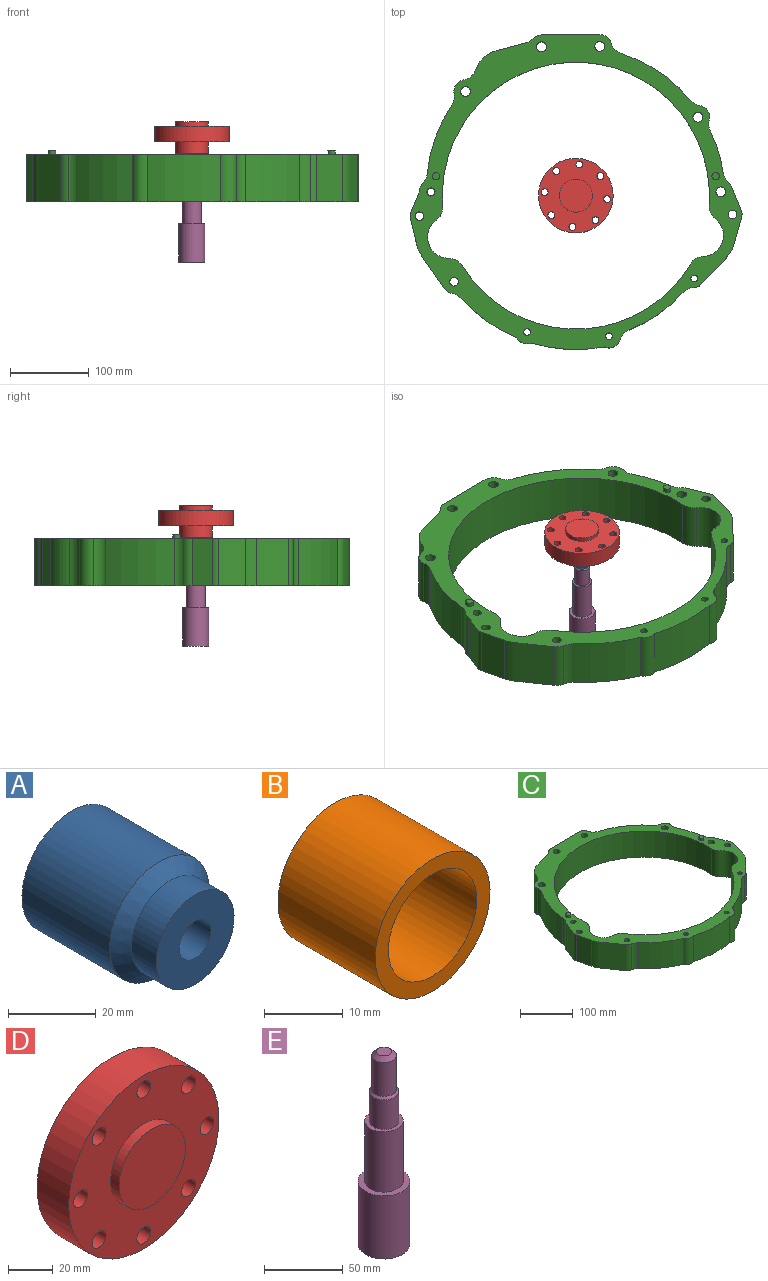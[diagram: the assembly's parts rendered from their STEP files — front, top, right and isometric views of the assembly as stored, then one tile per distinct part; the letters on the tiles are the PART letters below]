
ASSEMBLY  parts=5 mates=4
PART A: 10 faces, bbox 32x39.7x32 mm
  f0: plane 25x25mm, normal (0,-1,0), area 409.2mm2, adj f1,f9
  f1: cylinder r=5.1mm len=12.2mm, axis (0,-1,0), area 390.9mm2, adj f0,f2
  f2: plane 16.5x16.5mm, normal (0,1,0), area 132.1mm2, adj f1,f3
  f3: cylinder r=8.25mm len=16.5mm, axis (0,-1,0), area 518.4mm2, adj f2,f4
  f4: plane 20.65x20.65mm, normal (0,1,0), area 121.1mm2, adj f3,f5
  f5: cylinder r=10.33mm len=20.65mm, axis (0,-1,0), area 1135.3mm2, adj f4,f6
  f6: plane 32x32mm, normal (0,1,0), area 469.3mm2, adj f5,f7
  f7: cylinder r=16mm len=32mm, axis (0,-1,0), area 2835mm2, adj f6,f8
  f8: cone r=12.5mm half-angle=45deg, axis (0,1,0), area 443.2mm2, adj f7,f9
  f9: cylinder r=12.5mm len=25mm, axis (0,-1,0), area 628.3mm2, adj f0,f8
PART B: 4 faces, bbox 20.7x17.5x20.7 mm
  f0: cylinder r=10.33mm len=20.65mm, axis (0,-1,0), area 1135.3mm2, adj f1,f3
  f1: plane 20.65x20.65mm, normal (0,-1,0), area 136.4mm2, adj f0,f2
  f2: cylinder r=7.95mm len=17.5mm, axis (0,-1,0), area 874.1mm2, adj f1,f3
  f3: plane 20.65x20.65mm, normal (0,1,0), area 136.4mm2, adj f0,f2
PART C: 70 faces, bbox 422.8x401.2x65 mm
  f0: cylinder r=4.75mm len=55mm, axis (0,0,1), area 1641.5mm2, adj f62,f69
  f1: cylinder r=4.75mm len=55mm, axis (0,0,1), area 1641.5mm2, adj f62,f66
  f2: cylinder r=15mm len=60mm, axis (0,0,1), area 1165.5mm2, adj f3,f60,f62,f63
  f3: cylinder r=20mm len=60mm, axis (0,0,1), area 1172.4mm2, adj f2,f4,f62,f63
  f4: cylinder r=190mm len=88.05mm, axis (0,0,1), area 6458.4mm2, adj f3,f5,f62,f63
  f5: cylinder r=20mm len=60mm, axis (0,0,1), area 844.1mm2, adj f4,f6,f62,f63
  f6: cylinder r=15mm len=60mm, axis (0,0,1), area 1487.3mm2, adj f5,f7,f62,f63
  f7: cylinder r=20mm len=60mm, axis (0,0,1), area 844.1mm2, adj f6,f8,f62,f63
  f8: cylinder r=190mm len=60mm, axis (0,0,1), area 3403.2mm2, adj f7,f9,f62,f63
  f9: cylinder r=20mm len=60mm, axis (0,0,1), area 844.1mm2, adj f8,f10,f62,f63
  f10: cylinder r=15mm len=60mm, axis (0,0,1), area 421.9mm2, adj f9,f11,f62,f63
  f11: plane 60x30.04mm, normal (0.93,0.38,0), area 1944.6mm2, adj f10,f12,f62,f63
  f12: cylinder r=12mm len=60mm, axis (0,0,1), area 475.6mm2, adj f11,f13,f62,f63
  f13: plane 60x34.57mm, normal (0.96,-0.27,0), area 2155.9mm2, adj f12,f14,f62,f63
  f14: cylinder r=42mm len=60mm, axis (0,0,1), area 1222.6mm2, adj f13,f15,f62,f63
  f15: plane 60x34mm, normal (0.72,-0.69,0), area 2817.4mm2, adj f14,f16,f62,f63
  f16: cylinder r=11.25mm len=60mm, axis (0,0,1), area 534.3mm2, adj f15,f17,f62,f63
  f17: cylinder r=20mm len=60mm, axis (0,0,1), area 981.4mm2, adj f16,f18,f62,f63
  f18: cylinder r=184mm len=68.46mm, axis (0,0,1), area 5045.7mm2, adj f17,f19,f62,f63
  f19: cylinder r=20mm len=60mm, axis (0,0,1), area 1062.5mm2, adj f18,f20,f62,f63
  f20: cylinder r=15mm len=60mm, axis (0,0,1), area 1515.6mm2, adj f19,f21,f62,f63
  f21: cylinder r=196mm len=92.59mm, axis (0,0,1), area 5616.6mm2, adj f20,f22,f62,f63
  f22: cylinder r=15mm len=60mm, axis (0,0,1), area 1293.7mm2, adj f21,f23,f62,f63
  f23: cylinder r=196mm len=70.76mm, axis (0,0,1), area 5248.8mm2, adj f22,f24,f62,f63
  f24: cylinder r=20mm len=60mm, axis (0,0,1), area 810.5mm2, adj f23,f25,f62,f63
  f25: cylinder r=15mm len=60mm, axis (0,0,1), area 718.6mm2, adj f24,f26,f62,f63
  f26: plane 60x41.39mm, normal (-0.82,-0.57,0), area 3024.7mm2, adj f25,f27,f62,f63
  f27: cylinder r=42mm len=60mm, axis (0,0,1), area 924mm2, adj f26,f28,f62,f63
  f28: plane 60x33.81mm, normal (-0.97,-0.24,0), area 2088.9mm2, adj f27,f29,f62,f63
  f29: cylinder r=12mm len=60mm, axis (0,0,1), area 455.1mm2, adj f28,f30,f62,f63
  f30: plane 60x26.3mm, normal (-0.92,0.38,0), area 1707mm2, adj f29,f31,f62,f63
  f31: cylinder r=15mm len=60mm, axis (0,0,1), area 703.8mm2, adj f30,f32,f62,f63
  f32: cylinder r=20mm len=60mm, axis (0,0,1), area 824.6mm2, adj f31,f33,f62,f63
  f33: cylinder r=190mm len=87.63mm, axis (0,0,1), area 5639mm2, adj f32,f34,f62,f63
  f34: cylinder r=20mm len=60mm, axis (0,0,1), area 927.7mm2, adj f33,f35,f62,f63
  f35: cylinder r=15mm len=60mm, axis (0,0,1), area 1422.1mm2, adj f34,f36,f62,f63
  f36: cylinder r=20mm len=60mm, axis (0,0,1), area 1270.7mm2, adj f35,f37,f62,f63
  f37: cylinder r=38mm len=60mm, axis (0,0,1), area 2206.5mm2, adj f36,f38,f62,f63
  f38: plane 60x38.22mm, normal (-0.26,0.96,0), area 2376.4mm2, adj f37,f39,f62,f63
  f39: cylinder r=20mm len=60mm, axis (0,0,1), area 629.5mm2, adj f38,f40,f62,f63
  f40: cylinder r=15mm len=60mm, axis (0,0,1), area 703.9mm2, adj f39,f60,f62,f63
  f41: cylinder r=170mm len=340mm, axis (0,0,1), area 33542.8mm2, adj f42,f61,f62,f63
  f42: cylinder r=20mm len=60mm, axis (0,0,1), area 1223.2mm2, adj f41,f43,f62,f63
  f43: cylinder r=27mm len=60mm, axis (0,0,1), area 4072mm2, adj f42,f44,f62,f63
  f44: cylinder r=20mm len=60mm, axis (0,0,1), area 1223.2mm2, adj f43,f45,f62,f63
  f45: cylinder r=170mm len=290.68mm, axis (0,0,1), area 20920.2mm2, adj f44,f46,f62,f63
  f46: cylinder r=20mm len=60mm, axis (0,0,1), area 1181.3mm2, adj f45,f47,f62,f63
  f47: cylinder r=27mm len=60mm, axis (0,0,1), area 3948.7mm2, adj f46,f61,f62,f63
  f48: cylinder r=6.25mm len=60mm, axis (0,0,1), area 2356.2mm2, adj f62,f63
  f49: cylinder r=6.25mm len=60mm, axis (0,0,1), area 2356.2mm2, adj f62,f63
  f50: cylinder r=6.25mm len=60mm, axis (0,0,1), area 2356.2mm2, adj f62,f63
  f51: cylinder r=5.5mm len=60mm, axis (0,0,1), area 2073.5mm2, adj f62,f63
  f52: cylinder r=4.25mm len=60mm, axis (0,0,1), area 1602.2mm2, adj f62,f63
  f53: cylinder r=4.25mm len=60mm, axis (0,0,1), area 1602.2mm2, adj f62,f63
  f54: cylinder r=5.12mm len=60mm, axis (0,0,1), area 1932.1mm2, adj f62,f63
  f55: cylinder r=5.5mm len=60mm, axis (0,0,1), area 2073.5mm2, adj f62,f63
  f56: cylinder r=5.5mm len=60mm, axis (0,0,1), area 2073.5mm2, adj f62,f63
  f57: cylinder r=4.25mm len=60mm, axis (0,0,1), area 1602.2mm2, adj f62,f63
  f58: cylinder r=6.25mm len=60mm, axis (0,0,1), area 2356.2mm2, adj f62,f63
  f59: cylinder r=6.25mm len=60mm, axis (0,0,1), area 2356.2mm2, adj f62,f63
  f60: plane 74.32x60mm, normal (-0.01,1,0), area 4459.1mm2, adj f2,f40,f62,f63
  f61: cylinder r=20mm len=60mm, axis (0,0,1), area 1181.3mm2, adj f41,f47,f62,f63
  f62: plane 422.76x401.19mm, normal (0,0,-1), area 29010.6mm2, adj f0,f1,f2,f3,f4,f5,f6,f7
  f63: plane 422.76x401.19mm, normal (0,0,1), area 29010.6mm2, adj f2,f3,f4,f5,f6,f7,f8,f9
  f64: plane 9.5x9.5mm, normal (0,0,1), area 70.9mm2, adj f65
  f65: cylinder r=4.75mm len=9.5mm, axis (0,0,-1), area 149.2mm2, adj f63,f64
  f66: plane 9.5x9.5mm, normal (0,0,-1), area 70.9mm2, adj f1
  f67: plane 9.5x9.5mm, normal (0,0,1), area 70.9mm2, adj f68
  f68: cylinder r=4.75mm len=9.5mm, axis (0,0,-1), area 149.2mm2, adj f63,f67
  f69: plane 9.5x9.5mm, normal (0,0,-1), area 70.9mm2, adj f0
PART D: 19 faces, bbox 95x40x95 mm
  f0: cylinder r=14mm len=28mm, axis (0,1,0), area 351.9mm2, adj f1,f10
  f1: cone r=15.97mm half-angle=36.2deg, axis (0,1,0), area 315mm2, adj f0,f2
  f2: cylinder r=15.97mm len=31.95mm, axis (0,1,0), area 2308.6mm2, adj f1,f3
  f3: plane 42x42mm, normal (0,1,0), area 583.7mm2, adj f2,f4
  f4: cylinder r=21mm len=42mm, axis (0,1,0), area 1939.6mm2, adj f3,f5
  f5: plane 95x95mm, normal (0,1,0), area 5221.7mm2, adj f4,f6,f11,f12,f13,f14,f15,f16
  f6: cylinder r=47.5mm len=95mm, axis (0,1,0), area 5969mm2, adj f5,f7
  f7: plane 95x95mm, normal (0,-1,0), area 5221.7mm2, adj f6,f8,f11,f12,f13,f14,f15,f16
  f8: cylinder r=21mm len=42mm, axis (0,1,0), area 699.3mm2, adj f7,f9
  f9: plane 42x42mm, normal (0,-1,0), area 1385.4mm2, adj f8
  f10: plane 28x28mm, normal (0,1,0), area 615.8mm2, adj f0
  f11: cylinder r=4.38mm len=20mm, axis (0,1,0), area 549.8mm2, adj f5,f7
  f12: cylinder r=4.38mm len=20mm, axis (0,1,0), area 549.8mm2, adj f5,f7
  f13: cylinder r=4.38mm len=20mm, axis (0,1,0), area 549.8mm2, adj f5,f7
  f14: cylinder r=4.38mm len=20mm, axis (0,1,0), area 549.8mm2, adj f5,f7
  f15: cylinder r=4.38mm len=20mm, axis (0,1,0), area 549.8mm2, adj f5,f7
  f16: cylinder r=4.38mm len=20mm, axis (0,1,0), area 549.8mm2, adj f5,f7
  f17: cylinder r=4.38mm len=20mm, axis (0,1,0), area 549.8mm2, adj f5,f7
  f18: cylinder r=4.38mm len=20mm, axis (0,1,0), area 549.8mm2, adj f5,f7
PART E: 10 faces, bbox 33x33x150 mm
  f0: plane 33x33mm, normal (0,0,-1), area 855.3mm2, adj f7
  f1: plane 9.8x9.8mm, normal (0,0,1), area 75.4mm2, adj f9
  f2: cylinder r=7.9mm len=26.4mm, axis (0,0,1), area 1310.4mm2, adj f8,f9
  f3: cylinder r=9.5mm len=23mm, axis (0,0,1), area 1372.9mm2, adj f4,f8
  f4: plane 24.6x24.6mm, normal (0,0,1), area 191.8mm2, adj f3,f5
  f5: cylinder r=12.3mm len=46.9mm, axis (0,0,1), area 3624.6mm2, adj f4,f6
  f6: plane 33x33mm, normal (0,0,1), area 380mm2, adj f5,f7
  f7: cylinder r=16.5mm len=49.1mm, axis (0,0,1), area 5090.3mm2, adj f0,f6
  f8: cone r=6.5mm half-angle=45deg, axis (0,0,-1), area 123.7mm2, adj f2,f3
  f9: cone r=4.9mm half-angle=45deg, axis (0,0,-1), area 170.6mm2, adj f1,f2
PLACE A rot(axis=(-0.62,-0.55,0.55),116.4deg) t=(0,0,31.4)mm
PLACE B rot(axis=(1,0,0),90deg) t=(0,0,-8.3)mm
PLACE C at identity fixed
PLACE D rot(axis=(-0.53,0.6,-0.6),123.8deg) t=(0,0,1.7)mm
PLACE E at identity fixed
MATE cylindrical D.f0 <-> E.f9  axis (0,0,-1) through (0,0,13.2)mm
MATE slider B.f0 <-> E.f9  axis (0,0,1) through (0,0,9.2)mm
MATE cylindrical A.f1 <-> D.f0  axis (0,0,1) through (0,0,31.4)mm
MATE parallel C.f4 <-> D.f0  axis (0,0,1) through (0,0,0)mm
